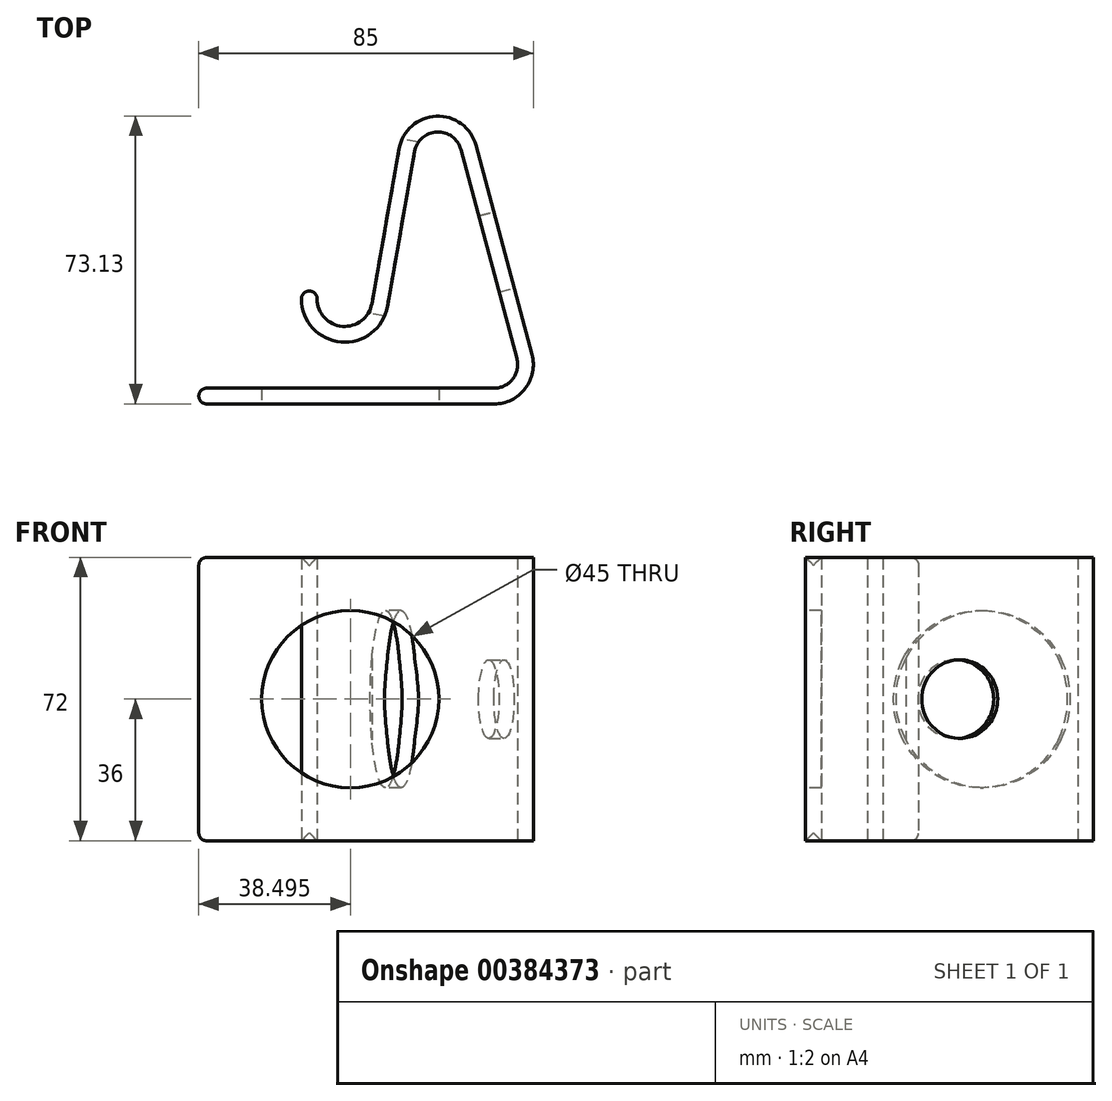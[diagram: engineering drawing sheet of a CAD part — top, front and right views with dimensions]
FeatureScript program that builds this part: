
annotation { "Feature Type Name" : "Feature", "Feature Type Description" : "" }
export const myFeature = defineFeature(function(context is Context, id is Id, definition is map)
    precondition{}
    {
        {
            var Q0;
            Q0=qCreatedBy(makeId("Top.planeOp"),FACE);
            var sketch = newSketch(context, id + "F0", { "sketchPlane" : qUnion([Q0])});
            skLineSegment(sketch, "E0", {"start": v(-16.8, -37.66) * mm, "end": v(-9.85, 1.74) * mm});
            skLineSegment(sketch, "E1", {"start": v(9.66, 2.59) * mm, "end": v(23.9, -50.54) * mm});
            skLineSegment(sketch, "E2", {"start": v(-60.76, -63.13) * mm, "end": v(14.24, -63.13) * mm});
            skArc(sketch, "E3", {"start": v(-9.85, 1.74) * mm, "mid": v(-0.44, 10) * mm, "end": v(9.66, 2.59) * mm});
            skArc(sketch, "E4", {"start": v(14.24, -63.13) * mm, "mid": v(22.17, -59.21) * mm, "end": v(23.9, -50.54) * mm});
            skArc(sketch, "E5", {"start": v(-16.8, -37.66) * mm, "mid": v(-24.3, -43.41) * mm, "end": v(-30.69, -36.44) * mm});
            skArc(sketch, "E6", {"start": v(-34.69, -36.44) * mm, "mid": v(-24.65, -47.4) * mm, "end": v(-12.85, -38.35) * mm});
            skLineSegment(sketch, "E7", {"start": v(-12.85, -38.35) * mm, "end": v(-5.9, 1.04) * mm});
            skLineSegment(sketch, "E8", {"start": v(5.8, 1.55) * mm, "end": v(20.03, -51.57) * mm});
            skArc(sketch, "E9", {"start": v(-5.9, 1.04) * mm, "mid": v(-0.26, 6) * mm, "end": v(5.8, 1.55) * mm});
            skArc(sketch, "E10", {"start": v(20.03, -51.57) * mm, "mid": v(19, -56.78) * mm, "end": v(14.24, -59.13) * mm});
            skLineSegment(sketch, "E11", {"start": v(14.24, -59.13) * mm, "end": v(-60.76, -59.13) * mm});
            skLineSegment(sketch, "E12", {"start": v(-60.76, -59.13) * mm, "end": v(-60.76, -63.13) * mm});
            skLineSegment(sketch, "E13", {"start": v(-34.69, -36.44) * mm, "end": v(-34.69, -34.44) * mm});
            skLineSegment(sketch, "E14", {"start": v(-34.69, -34.44) * mm, "end": v(-30.69, -34.44) * mm});
            skLineSegment(sketch, "E15", {"start": v(-30.69, -36.44) * mm, "end": v(-30.69, -34.44) * mm});
            skSolve(sketch);
        }
        {
            var Q0;
            Q0=makeQuery(id+"F0.imprint","IMPRINT",FACE,{"disambiguationData":[TD([[makeQuery(id+"F0.imprint","IMPRINT",EDGE,{"derivedFrom":sQuery(id+"F0.wireOp",EDGE,"E0")}),-1.0]])]});
            extrude(context, id + "F1", {"entities" : qUnion([Q0]), "depth" : 72 * mm});
        }
        {
            var Q0;
            Q0=makeQuery(id+"F1.opExtrude","SWEPT_FACE",FACE,{"disambiguationData":[OSD([sQuery(id+"F0.wireOp",EDGE,"E14")])]});
            fillet(context, id + "F2", {"entities" : qUnion([Q0]), "radius" : 2 * mm, "tangentPropagation" : true, "allowEdgeOverflow" : false});
        }
        {
            var Q0;
            Q0=makeQuery(id+"F1.opExtrude","SWEPT_FACE",FACE,{"disambiguationData":[OSD([sQuery(id+"F0.wireOp",EDGE,"E12")])]});
            fillet(context, id + "F3", {"entities" : qUnion([Q0]), "radius" : 2 * mm, "tangentPropagation" : true, "allowEdgeOverflow" : false});
        }
        {
            var Q0;
            Q0=makeQuery(id+"F1.opExtrude","SWEPT_FACE",FACE,{"disambiguationData":[OSD([sQuery(id+"F0.wireOp",EDGE,"E1")])]});
            var sketch = newSketch(context, id + "F4", { "sketchPlane" : qUnion([Q0])});
            skLineSegment(sketch, "E16", {"start": v(0, 36) * mm, "end": v(-55, 36) * mm, "construction": true});
            skLineSegment(sketch, "E17", {"start": v(-27.5, 72) * mm, "end": v(-27.5, 0) * mm, "construction": true});
            skCircle(sketch, "E18", {"center": v(-27.5, 36) * mm, "radius": 10 * mm});
            skSolve(sketch);
        }
        {
            var Q0;
            Q0=qSketchRegion(id+"F4",true);
            extrude(context, id + "F5", {"entities" : qUnion([Q0]), "operationType" : NewBodyOperationType.REMOVE, "oppositeDirection" : true, "depth" : 5 * mm});
        }
        {
            var Q0;
            Q0=makeQuery(id+"F1.opExtrude","SWEPT_FACE",FACE,{"disambiguationData":[OSD([sQuery(id+"F0.wireOp",EDGE,"E0")])]});
            var sketch = newSketch(context, id + "F6", { "sketchPlane" : qUnion([Q0])});
            skLineSegment(sketch, "E19", {"start": v(40, 36) * mm, "end": v(0, 36) * mm, "construction": true});
            skLineSegment(sketch, "E20", {"start": v(20, 72) * mm, "end": v(20, 0) * mm, "construction": true});
            skCircle(sketch, "E21", {"center": v(20, 36) * mm, "radius": 22.5 * mm});
            skSolve(sketch);
        }
        {
            var Q0;
            Q0=qSketchRegion(id+"F6",true);
            extrude(context, id + "F7", {"entities" : qUnion([Q0]), "operationType" : NewBodyOperationType.REMOVE, "oppositeDirection" : true, "depth" : 5 * mm});
        }
        {
            var Q0;
            Q0=makeQuery(id+"F1.opExtrude","SWEPT_FACE",FACE,{"disambiguationData":[OSD([sQuery(id+"F0.wireOp",EDGE,"E2")])]});
            var sketch = newSketch(context, id + "F8", { "sketchPlane" : qUnion([Q0])});
            skLineSegment(sketch, "E22", {"start": v(-58.76, 36) * mm, "end": v(14.24, 36) * mm, "construction": true});
            skLineSegment(sketch, "E23", {"start": v(-22.26, 0) * mm, "end": v(-22.26, 72) * mm, "construction": true});
            skCircle(sketch, "E24", {"center": v(-22.26, 36) * mm, "radius": 22.5 * mm});
            skSolve(sketch);
        }
        {
            var Q0;
            Q0=qSketchRegion(id+"F8",true);
            extrude(context, id + "F9", {"entities" : qUnion([Q0]), "operationType" : NewBodyOperationType.REMOVE, "oppositeDirection" : true, "depth" : 5 * mm});
        }
    });
